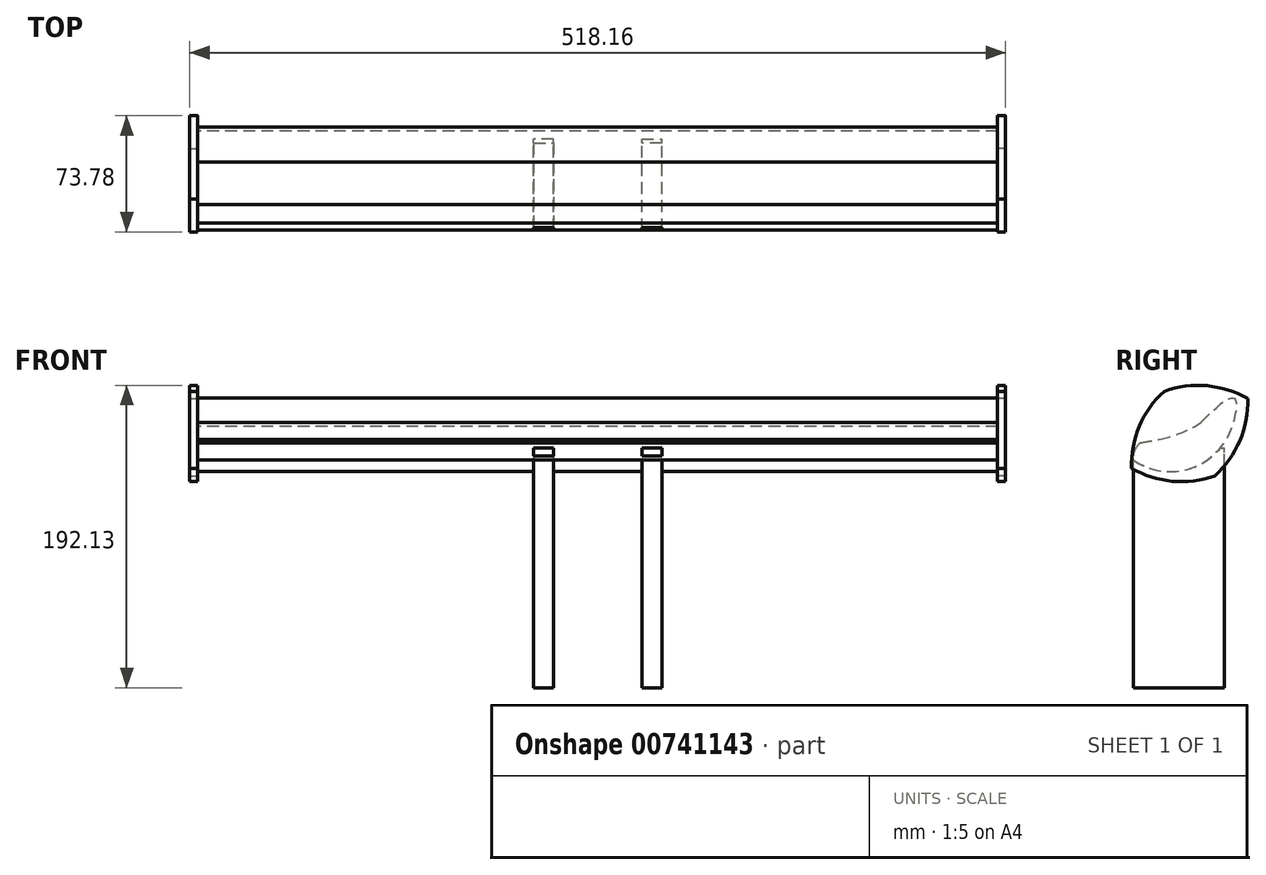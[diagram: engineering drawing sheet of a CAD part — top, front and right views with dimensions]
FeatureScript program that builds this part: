
annotation { "Feature Type Name" : "Feature", "Feature Type Description" : "" }
export const myFeature = defineFeature(function(context is Context, id is Id, definition is map)
    precondition{}
    {
        {
            var Q0;
            Q0=qCreatedBy(makeId("Right.planeOp"),FACE);
            var sketch = newSketch(context, id + "F0", { "sketchPlane" : qUnion([Q0])});
            skPoint(sketch, "E0", {"position": v(0, 0) * mm});
            skPoint(sketch, "E1", {"position": v(-5.47, 26.28) * mm});
            skArc(sketch, "E2", {"start": v(-28.99, -7.7) * mm, "mid": v(7.82, -12.85) * mm, "end": v(33.88, 13.66) * mm});
            skFitSpline(sketch, "E3", {"points": [v(-28.99, -7.7) * mm, v(-12.57, 5.38) * mm], "startDerivative": vector(-50.54, 23.1) * mm, "endDerivative": vector(87.53, 16.14) * mm});
            skFitSpline(sketch, "E4", {"points": [v(14.14, 16.15) * mm, v(33.88, 13.66) * mm], "startDerivative": vector(33.8, 33.9) * mm, "endDerivative": vector(-27.82, -96.12) * mm});
            skArc(sketch, "E5", {"start": v(-24.53, 3.18) * mm, "mid": v(-28.12, -1.7) * mm, "end": v(-28.99, -7.7) * mm});
            skFitSpline(sketch, "E6", {"points": [v(-12.57, 5.38) * mm, v(14.14, 16.15) * mm], "startDerivative": vector(30.82, 6.5) * mm, "endDerivative": vector(22.68, 15.07) * mm});
            skSolve(sketch);
        }
        {
            var Q0;
            Q0=makeQuery(id+"F0.imprint","IMPRINT",FACE,{"disambiguationData":[TD([[makeQuery(id+"F0.imprint","IMPRINT",EDGE,{"derivedFrom":sQuery(id+"F0.wireOp",EDGE,"E2")}),1.0]])]});
            extrude(context, id + "F1", {"entities" : qUnion([Q0]), "depth" : 254 * mm, "offsetDistance" : 25.4 * mm});
        }
        {
            var Q0;
            Q0=makeQuery(id+"F1.opExtrude","CAP_FACE",FACE,{"disambiguationData":[OSD([sQuery(id+"F0.wireOp",EDGE,"E2"),sQuery(id+"F0.wireOp",EDGE,"E3"),sQuery(id+"F0.wireOp",EDGE,"E4"),sQuery(id+"F0.wireOp",EDGE,"E5"),sQuery(id+"F0.wireOp",EDGE,"E6")])],"isStart":false});
            var sketch = newSketch(context, id + "F2", { "sketchPlane" : qUnion([Q0])});
            skLineSegment(sketch, "E7", {"start": v(-53.41, 10.86) * mm, "end": v(-20.06, -44.79) * mm});
            skLineSegment(sketch, "E8", {"start": v(-53.41, 10.86) * mm, "end": v(33.73, 63.1) * mm});
            skLineSegment(sketch, "E9", {"start": v(-20.06, -44.79) * mm, "end": v(70.61, 9.56) * mm});
            skPoint(sketch, "E10.end.orphan", {"position": v(65.82, 9.56) * mm});
            skLineSegment(sketch, "E11", {"start": v(33.73, 63.1) * mm, "end": v(67.09, 7.44) * mm});
            skSolve(sketch);
        }
        {
            var Q0;
            Q0 = qSketchRegion(id + "F2", true);
            extrude(context, id + "F3", {"entities" : qUnion([Q0]), "depth" : 5.08 * mm, "offsetDistance" : 25.4 * mm});
        }
        {
            var Q0;
            Q0=qCreatedBy(makeId("Top.planeOp"),FACE);
            var sketch = newSketch(context, id + "F4", { "sketchPlane" : qUnion([Q0])});
            skLineSegment(sketch, "E12.bottom", {"start": v(28.06, -28.97) * mm, "end": v(40.73, -28.97) * mm});
            skLineSegment(sketch, "E12.top", {"start": v(28.06, 28.97) * mm, "end": v(40.73, 28.97) * mm});
            skLineSegment(sketch, "E12.left", {"start": v(28.06, -28.97) * mm, "end": v(28.06, 28.97) * mm});
            skLineSegment(sketch, "E12.right", {"start": v(40.73, -28.97) * mm, "end": v(40.73, 28.97) * mm});
            skPoint(sketch, "E12.middle", {"position": v(34.4, 0) * mm});
            skSolve(sketch);
        }
        {
            var Q0;
            Q0 = qSketchRegion(id + "F4", true);
            extrude(context, id + "F5", {"entities" : qUnion([Q0]), "oppositeDirection" : true, "depth" : 152.4 * mm, "offsetDistance" : 25.4 * mm});
        }
        {
            var Q0;
            Q0=makeQuery(id+"F3.opExtrude","SWEPT_EDGE",EDGE,{"disambiguationData":[OSD([sQuery(id+"F2.wireOp",EDGE,"E7"),sQuery(id+"F2.wireOp",EDGE,"E9")])]});
            var Q1;
            Q1=makeQuery(id+"F3.opExtrude","SWEPT_EDGE",EDGE,{"disambiguationData":[OSD([sQuery(id+"F2.wireOp",EDGE,"E7"),sQuery(id+"F2.wireOp",EDGE,"E8")])]});
            var Q2;
            Q2=makeQuery(id+"F3.opExtrude","SWEPT_EDGE",EDGE,{"disambiguationData":[OSD([sQuery(id+"F2.wireOp",EDGE,"E8"),sQuery(id+"F2.wireOp",EDGE,"E11")])]});
            var Q3;
            Q3=makeQuery(id+"F3.opExtrude","SWEPT_EDGE",EDGE,{"disambiguationData":[OSD([sQuery(id+"F2.wireOp",EDGE,"E9"),sQuery(id+"F2.wireOp",EDGE,"E11")])]});
            fillet(context, id + "F6", {"entities" : qUnion([Q0, Q1, Q2, Q3]), "radius" : 62.83 * mm, "tangentPropagation" : true, "allowEdgeOverflow" : false});
        }
        {
            var Q0;
            Q0=makeQuery(id+"F1.opExtrude","SWEPT_BODY",BODY,{"disambiguationData":[OSD([sQuery(id+"F0.wireOp",EDGE,"E2"),sQuery(id+"F0.wireOp",EDGE,"E3"),sQuery(id+"F0.wireOp",EDGE,"E4"),sQuery(id+"F0.wireOp",EDGE,"E5"),sQuery(id+"F0.wireOp",EDGE,"E6")])]});
            var Q1;
            Q1=makeQuery(id+"F3.opExtrude","SWEPT_BODY",BODY,{"disambiguationData":[OSD([sQuery(id+"F2.wireOp",EDGE,"E7"),sQuery(id+"F2.wireOp",EDGE,"E8"),sQuery(id+"F2.wireOp",EDGE,"E9"),sQuery(id+"F2.wireOp",EDGE,"E11")])]});
            var Q2;
            Q2=makeQuery(id+"F5.opExtrude","SWEPT_BODY",BODY,{"disambiguationData":[OSD([sQuery(id+"F4.wireOp",EDGE,"E12.bottom"),sQuery(id+"F4.wireOp",EDGE,"E12.top"),sQuery(id+"F4.wireOp",EDGE,"E12.left"),sQuery(id+"F4.wireOp",EDGE,"E12.right")])]});
            var Q3;
            Q3=makeQuery(id+"F1.opExtrude","CAP_FACE",FACE,{"disambiguationData":[OSD([sQuery(id+"F0.wireOp",EDGE,"E2"),sQuery(id+"F0.wireOp",EDGE,"E3"),sQuery(id+"F0.wireOp",EDGE,"E4"),sQuery(id+"F0.wireOp",EDGE,"E5"),sQuery(id+"F0.wireOp",EDGE,"E6")])],"isStart":true});
            mirror(context, id + "F7", {"operationType" : NewBodyOperationType.ADD, "entities" : qUnion([Q0, Q1, Q2]), "mirrorPlane" : qUnion([Q3])});
        }
    });
